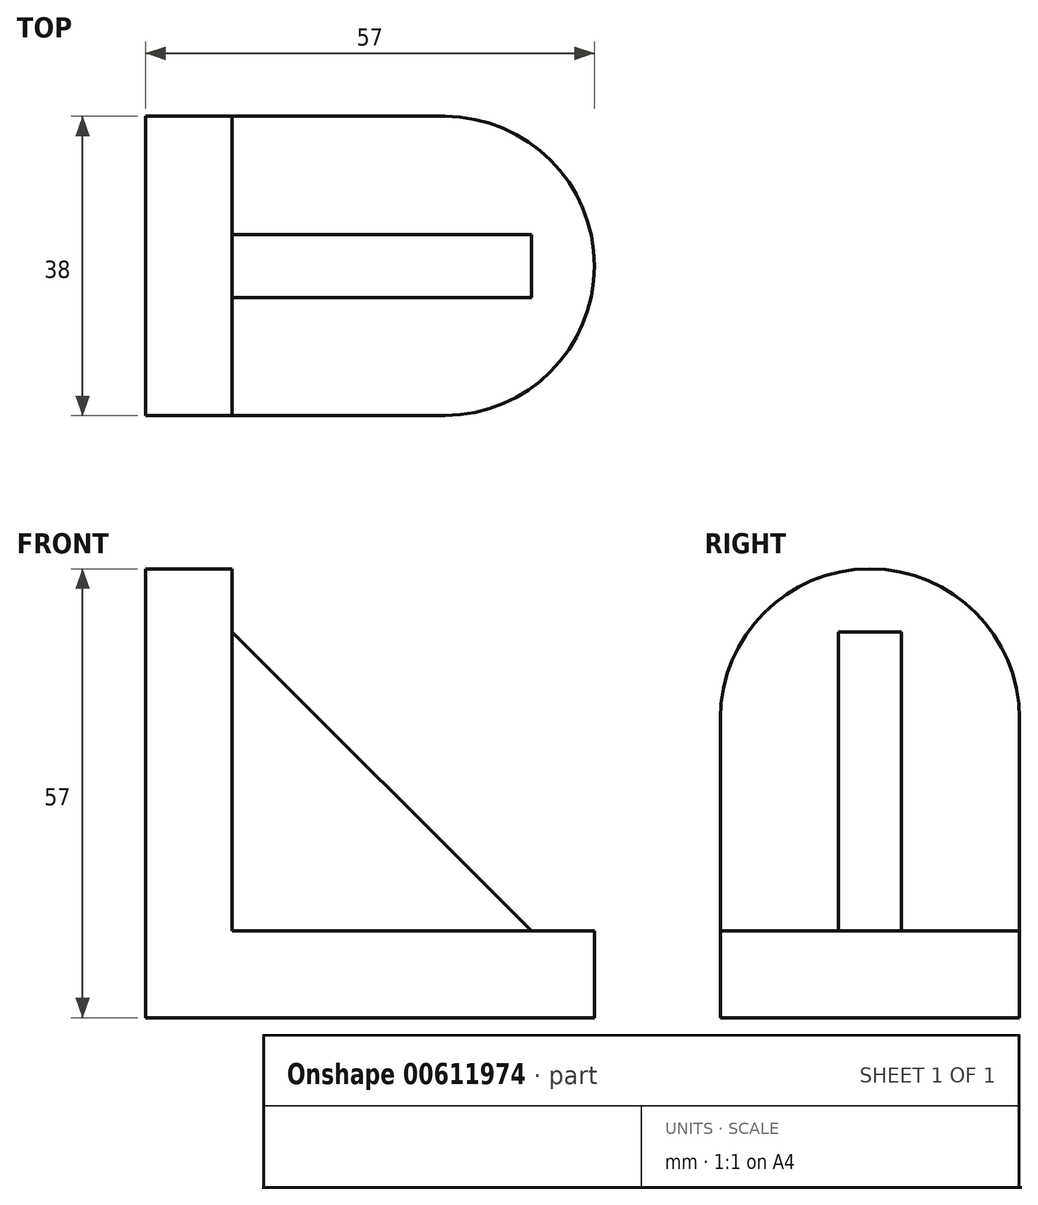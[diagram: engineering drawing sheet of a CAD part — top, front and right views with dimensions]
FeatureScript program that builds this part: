
annotation { "Feature Type Name" : "Feature", "Feature Type Description" : "" }
export const myFeature = defineFeature(function(context is Context, id is Id, definition is map)
    precondition{}
    {
        {
            var Q0;
            Q0=qCreatedBy(makeId("Right.planeOp"),FACE);
            var sketch = newSketch(context, id + "F0", { "sketchPlane" : qUnion([Q0])});
            skLineSegment(sketch, "E0.bottom", {"start": v(0, 0) * mm, "end": v(-38, 0) * mm});
            skLineSegment(sketch, "E0.top", {"start": v(-19, 57) * mm, "end": v(-19, 57) * mm});
            skLineSegment(sketch, "E0.left", {"start": v(0, 0) * mm, "end": v(0, 38) * mm});
            skLineSegment(sketch, "E0.right", {"start": v(-38, 0) * mm, "end": v(-38, 38) * mm});
            skPoint(sketch, "E1.visualSharp", {"position": v(-38, 57) * mm});
            skArc(sketch, "E1.filletArc", {"start": v(-19, 57) * mm, "mid": v(-32.44, 51.44) * mm, "end": v(-38, 38) * mm});
            skPoint(sketch, "E2.visualSharp", {"position": v(0, 57) * mm});
            skArc(sketch, "E2.filletArc", {"start": v(0, 38) * mm, "mid": v(-5.56, 51.44) * mm, "end": v(-19, 57) * mm});
            skSolve(sketch);
        }
        {
            var Q0;
            Q0=makeQuery(id+"F0.imprint","IMPRINT",FACE,{"disambiguationData":[TD([[makeQuery(id+"F0.imprint","IMPRINT",EDGE,{"derivedFrom":sQuery(id+"F0.wireOp",EDGE,"E0.bottom")}),-1.0]])]});
            extrude(context, id + "F1", {"entities" : qUnion([Q0]), "depth" : 11 * mm, "offsetDistance" : 25.4 * mm});
        }
        {
            var Q0;
            Q0=qCreatedBy(makeId("Top.planeOp"),FACE);
            var sketch = newSketch(context, id + "F2", { "sketchPlane" : qUnion([Q0])});
            skLineSegment(sketch, "E3.bottom", {"start": v(0, 0) * mm, "end": v(38, 0) * mm});
            skLineSegment(sketch, "E3.top", {"start": v(0, -38) * mm, "end": v(38, -38) * mm});
            skLineSegment(sketch, "E3.left", {"start": v(0, 0) * mm, "end": v(0, -38) * mm});
            skLineSegment(sketch, "E3.right", {"start": v(57, -19) * mm, "end": v(57, -19) * mm});
            skPoint(sketch, "E4.visualSharp", {"position": v(57, -38) * mm});
            skArc(sketch, "E4.filletArc", {"start": v(38, -38) * mm, "mid": v(51.44, -32.44) * mm, "end": v(57, -19) * mm});
            skPoint(sketch, "E5.visualSharp", {"position": v(57, 0) * mm});
            skArc(sketch, "E5.filletArc", {"start": v(57, -19) * mm, "mid": v(51.44, -5.56) * mm, "end": v(38, 0) * mm});
            skSolve(sketch);
        }
        {
            var Q0;
            Q0=makeQuery(id+"F2.imprint","IMPRINT",FACE,{"disambiguationData":[TD([[makeQuery(id+"F2.imprint","IMPRINT",EDGE,{"derivedFrom":sQuery(id+"F2.wireOp",EDGE,"E3.bottom")}),-1.0]])]});
            extrude(context, id + "F3", {"entities" : qUnion([Q0]), "operationType" : NewBodyOperationType.ADD, "depth" : 11 * mm, "offsetDistance" : 25.4 * mm});
        }
        {
            var Q0;
            Q0=makeQuery(id+"F3.boolean.opBoolean","INTERSECT",EDGE,{"derivedFrom":[makeQuery(id+"F1.opExtrude","CAP_FACE",FACE,{"disambiguationData":[OSD([sQuery(id+"F0.wireOp",EDGE,"E0.bottom"),sQuery(id+"F0.wireOp",EDGE,"E0.left"),sQuery(id+"F0.wireOp",EDGE,"E0.right"),sQuery(id+"F0.wireOp",EDGE,"E1.filletArc"),sQuery(id+"F0.wireOp",EDGE,"E2.filletArc")])],"isStart":false}),makeQuery(id+"F3.opExtrude","CAP_FACE",FACE,{"disambiguationData":[OSD([sQuery(id+"F2.wireOp",EDGE,"E3.bottom"),sQuery(id+"F2.wireOp",EDGE,"E3.top"),sQuery(id+"F2.wireOp",EDGE,"E3.left"),sQuery(id+"F2.wireOp",EDGE,"E4.filletArc"),sQuery(id+"F2.wireOp",EDGE,"E5.filletArc")])],"isStart":false})]});
            cPoint(context, id + "F4", {"entities" : qUnion([Q0]), "parameter" : 0.5});
        }
        {
            var Q0;
            Q0=makeQuery(id+"F3.opExtrude","CAP_EDGE",EDGE,{"disambiguationData":[OSD([sQuery(id+"F2.wireOp",EDGE,"E4.filletArc"),sQuery(id+"F2.wireOp",EDGE,"E5.filletArc")])],"isStart":false});
            cPoint(context, id + "F5", {"entities" : qUnion([Q0]), "parameter" : 0.5});
        }
        {
            var Q0;
            Q0=makeQuery(id+"F1.opExtrude","CAP_EDGE",EDGE,{"disambiguationData":[OSD([sQuery(id+"F0.wireOp",EDGE,"E1.filletArc"),sQuery(id+"F0.wireOp",EDGE,"E2.filletArc")])],"isStart":false});
            cPoint(context, id + "F6", {"entities" : qUnion([Q0]), "parameter" : 0.5});
        }
        {
            var Q0;
            Q0 = qCreatedBy(id + "F4" ,VERTEX);
            var Q1;
            Q1 = qCreatedBy(id + "F5" ,VERTEX);
            var Q2;
            Q2 = qCreatedBy(id + "F6" ,VERTEX);
            cPlane(context, id + "F7", {"entities" : qUnion([Q0, Q1, Q2]), "cplaneType" : CPlaneType.THREE_POINT, "offset" : 25.4 * mm, "width" : 152.4 * mm, "height" : 152.4 * mm});
        }
        {
            var Q0;
            Q0=qCreatedBy(id+"F7.planeOp",FACE);
            var sketch = newSketch(context, id + "F8", { "sketchPlane" : qUnion([Q0])});
            skLineSegment(sketch, "E6", {"start": v(0, 0) * mm, "end": v(-49, 0) * mm});
            skLineSegment(sketch, "E7", {"start": v(-49, 0) * mm, "end": v(-49, 11) * mm});
            skLineSegment(sketch, "E8", {"start": v(-49, 11) * mm, "end": v(-11, 11) * mm});
            skLineSegment(sketch, "E9", {"start": v(-11, 11) * mm, "end": v(-11, 49) * mm});
            skLineSegment(sketch, "E10", {"start": v(-11, 49) * mm, "end": v(0, 49) * mm});
            skLineSegment(sketch, "E11", {"start": v(0, 49) * mm, "end": v(0, 0) * mm});
            skLineSegment(sketch, "E12", {"start": v(-11, 49) * mm, "end": v(-49, 11) * mm});
            skSolve(sketch);
        }
        {
            var Q0;
            Q0=makeQuery(id+"F8.imprint","IMPRINT",FACE,{"disambiguationData":[TD([[makeQuery(id+"F8.imprint","IMPRINT",EDGE,{"derivedFrom":sQuery(id+"F8.wireOp",EDGE,"E8")}),1.0]])]});
            extrude(context, id + "F9", {"entities" : qUnion([Q0]), "operationType" : NewBodyOperationType.ADD, "depth" : 8 * mm, "offsetDistance" : 25.4 * mm, "symmetric" : true});
        }
    });
